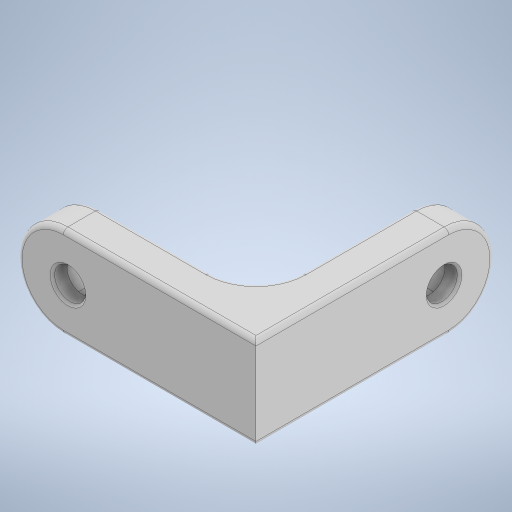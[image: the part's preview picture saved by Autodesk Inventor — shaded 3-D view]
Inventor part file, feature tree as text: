
AUTODESK INVENTOR PART (.ipt)
format: ipt  version: 2024.2 (Build 282272000, 272)  size: 315,392 bytes
history: native  units: mm
features: extrude x6, fillet x3, chamfer x1, projected_geometry x1
ambient origin geometry x8: Origin, YZ Plane, XZ Plane, XY Plane, X Axis, Y Axis, Z Axis, Center Point
bodies: Solid1 (feature_tree)
feature tree (11):
  extrude  "Extrusion1"  Depth=10.0mm
  extrude  "Extrusion2"  Depth=26.0mm
  extrude  "Extrusion3"  Depth=4.0mm TaperAngle=0.0deg
  extrude  "Extrusion4"  Depth=26.0mm
  extrude  "Extrusion5"  Depth=4.0mm TaperAngle=0.0deg
  extrude  "Extrusion6"  Depth=5.7mm
  fillet  "Fillet1"  Radius=5.5mm
  fillet  "Fillet2"  Radius=2.4mm
  fillet  "Fillet3"  Radius=3.4mm
  chamfer  "Chamfer1"  Distance=2.4mm
  projected_geometry  "Projected Loop1"
